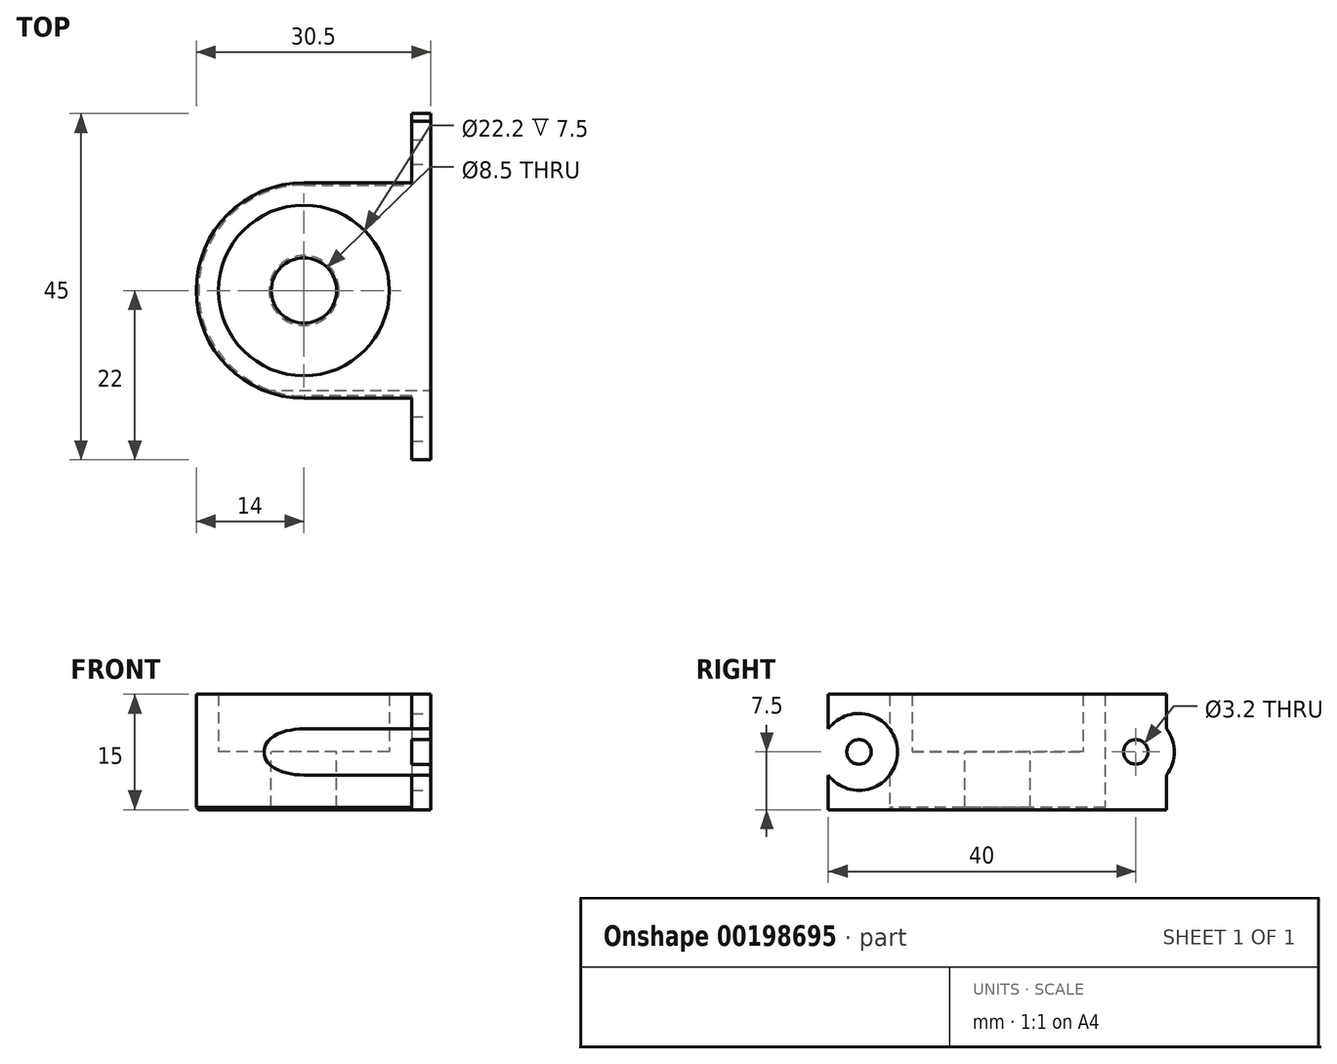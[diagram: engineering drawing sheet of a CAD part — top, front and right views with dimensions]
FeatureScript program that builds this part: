
annotation { "Feature Type Name" : "Feature", "Feature Type Description" : "" }
export const myFeature = defineFeature(function(context is Context, id is Id, definition is map)
    precondition{}
    {
        {
            var Q0;
            Q0=qCreatedBy(makeId("Top.planeOp"),FACE);
            var sketch = newSketch(context, id + "F0", { "sketchPlane" : qUnion([Q0])});
            skCircle(sketch, "E0", {"center": v(0, 0) * mm, "radius": 11.1 * mm});
            skCircle(sketch, "E1.0", {"center": v(0, 0) * mm, "radius": 14 * mm});
            skLineSegment(sketch, "E2", {"start": v(0, 14) * mm, "end": v(14, 14) * mm});
            skLineSegment(sketch, "E3", {"start": v(14, 14) * mm, "end": v(14, 22) * mm});
            skLineSegment(sketch, "E4", {"start": v(14, 22) * mm, "end": v(16.5, 22) * mm});
            skLineSegment(sketch, "E5", {"start": v(16.5, 22) * mm, "end": v(16.5, 0) * mm});
            skLineSegment(sketch, "E6.MirrorCS", {"start": v(16.5, -22) * mm, "end": v(16.5, 0) * mm});
            skLineSegment(sketch, "E7.MirrorCS", {"start": v(14, -14) * mm, "end": v(14, -22) * mm});
            skLineSegment(sketch, "E8.MirrorCS", {"start": v(14, -22) * mm, "end": v(16.5, -22) * mm});
            skLineSegment(sketch, "E9.MirrorCS", {"start": v(0, -14) * mm, "end": v(14, -14) * mm});
            skCircle(sketch, "E10", {"center": v(0, 0) * mm, "radius": 4.25 * mm});
            skSolve(sketch);
        }
        {
            var Q0;
            Q0=makeQuery(id+"F0.imprint","IMPRINT",FACE,{"disambiguationData":[TD([[makeQuery(id+"F0.imprint","IMPRINT",EDGE,{"derivedFrom":sQuery(id+"F0.wireOp",EDGE,"E0")}),-1.0]])]});
            var Q1;
            {var subQ0=sQuery(id+"F0.wireOp",EDGE,"E2");Q1=makeQuery(id+"F0.imprint","IMPRINT",FACE,{"disambiguationData":[TD([[makeQuery(id+"F0.imprint","IMPRINT",EDGE,{"derivedFrom":subQ0}),-1.0]])]});}
            extrude(context, id + "F1", {"entities" : qUnion([Q0, Q1]), "depth" : 7.5 * mm});
        }
        {
            var Q0;
            {var subQ0=sQuery(id+"F0.wireOp",EDGE,"E2");Q0=makeQuery(id+"F0.imprint","IMPRINT",FACE,{"disambiguationData":[TD([[makeQuery(id+"F0.imprint","IMPRINT",EDGE,{"derivedFrom":subQ0}),-1.0]])]});}
            var Q1;
            Q1=makeQuery(id+"F0.imprint","IMPRINT",FACE,{"disambiguationData":[TD([[makeQuery(id+"F0.imprint","IMPRINT",EDGE,{"derivedFrom":sQuery(id+"F0.wireOp",EDGE,"E0")}),-1.0]])]});
            var Q2;
            Q2=makeQuery(id+"F0.imprint","IMPRINT",FACE,{"disambiguationData":[TD([[makeQuery(id+"F0.imprint","IMPRINT",EDGE,{"derivedFrom":sQuery(id+"F0.wireOp",EDGE,"E0")}),1.0]])]});
            extrude(context, id + "F2", {"entities" : qUnion([Q0, Q1, Q2]), "operationType" : NewBodyOperationType.ADD, "oppositeDirection" : true, "depth" : 7.5 * mm});
        }
        {
            var Q0;
            {var subQ0=sQuery(id+"F0.wireOp",EDGE,"E6.MirrorCS");var subQ1=sQuery(id+"F0.wireOp",EDGE,"E5");Q0=makeQuery(id+"F2.boolean.opBoolean","MERGE",FACE,{"derivedFrom":[makeQuery(id+"F1.opExtrude","SWEPT_FACE",FACE,{"disambiguationData":[OSD([subQ1,subQ0])]}),makeQuery(id+"F2.opExtrude","SWEPT_FACE",FACE,{"disambiguationData":[OSD([subQ1,subQ0])]})]});}
            var sketch = newSketch(context, id + "F3", { "sketchPlane" : qUnion([Q0])});
            skLineSegment(sketch, "E11.0", {"start": v(14, 7.5) * mm, "end": v(22, 7.5) * mm, "construction": true});
            skLineSegment(sketch, "E12.0", {"start": v(14, -7.5) * mm, "end": v(22, -7.5) * mm, "construction": true});
            skLineSegment(sketch, "E13", {"start": v(18, -7.5) * mm, "end": v(18, 7.5) * mm, "construction": true});
            skCircle(sketch, "E14", {"center": v(18, 0) * mm, "radius": 1.6 * mm});
            skCircle(sketch, "E15.MirrorC", {"center": v(-18, 0) * mm, "radius": 1.6 * mm});
            skCircle(sketch, "E16", {"center": v(18, 0) * mm, "radius": 5 * mm});
            skCircle(sketch, "E17.MirrorC", {"center": v(-18, 0) * mm, "radius": 5 * mm});
            skSolve(sketch);
        }
        {
            var Q0;
            Q0=makeQuery(id+"F3.imprint","IMPRINT",FACE,{"disambiguationData":[TD([[makeQuery(id+"F3.imprint","IMPRINT",EDGE,{"derivedFrom":sQuery(id+"F3.wireOp",EDGE,"E14")}),1.0]])]});
            var Q1;
            Q1=makeQuery(id+"F3.imprint","IMPRINT",FACE,{"disambiguationData":[TD([[makeQuery(id+"F3.imprint","IMPRINT",EDGE,{"derivedFrom":sQuery(id+"F3.wireOp",EDGE,"E15.MirrorC")}),-1.0]])]});
            extrude(context, id + "F4", {"entities" : qUnion([Q0, Q1]), "operationType" : NewBodyOperationType.REMOVE, "endBound" : BoundingType.THROUGH_ALL, "oppositeDirection" : true, "depth" : 25 * mm});
        }
        {
            var Q0;
            Q0=makeQuery(id+"F2.opExtrude","CAP_FACE",FACE,{"disambiguationData":[OSD([sQuery(id+"F0.wireOp",EDGE,"E1.0"),sQuery(id+"F0.wireOp",EDGE,"E2"),sQuery(id+"F0.wireOp",EDGE,"E3"),sQuery(id+"F0.wireOp",EDGE,"E4"),sQuery(id+"F0.wireOp",EDGE,"E5"),sQuery(id+"F0.wireOp",EDGE,"E6.MirrorCS"),sQuery(id+"F0.wireOp",EDGE,"E7.MirrorCS"),sQuery(id+"F0.wireOp",EDGE,"E8.MirrorCS"),sQuery(id+"F0.wireOp",EDGE,"E9.MirrorCS"),sQuery(id+"F0.wireOp",EDGE,"E10")])],"isStart":false});
            chamfer(context, id + "F5", {"entities" : qUnion([Q0]), "width" : 0.3 * mm});
        }
        {
            var Q0;
            {var subQ0=sQuery(id+"F3.wireOp",EDGE,"E16");var subQ1=sQuery(id+"F0.wireOp",EDGE,"E5");var subQ2=sQuery(id+"F0.wireOp",EDGE,"E4");var subQ3=makeQuery(id+"F2.boolean.opBoolean","MERGE",EDGE,{"derivedFrom":[makeQuery(id+"F1.opExtrude","SWEPT_EDGE",EDGE,{"disambiguationData":[OSD([subQ2,subQ1])]}),makeQuery(id+"F2.opExtrude","SWEPT_EDGE",EDGE,{"disambiguationData":[OSD([subQ2,subQ1])]})]});var subQ4=makeQuery(id+"F3.imprint","INTERSECT",VERTEX,{"disambiguationData":[OD(0.0)],"derivedFrom":[subQ3,subQ0]});Q0=makeQuery(id+"F3.imprint","IMPRINT",FACE,{"disambiguationData":[TD([[makeQuery(id+"F3.imprint","IMPRINT",EDGE,{"disambiguationData":[TD([[subQ4,1.0]])],"derivedFrom":subQ0}),1.0]])]});}
            var Q1;
            {var subQ0=sQuery(id+"F3.wireOp",EDGE,"E17.MirrorC");var subQ1=sQuery(id+"F0.wireOp",EDGE,"E8.MirrorCS");var subQ2=sQuery(id+"F0.wireOp",EDGE,"E6.MirrorCS");var subQ3=makeQuery(id+"F2.boolean.opBoolean","MERGE",EDGE,{"derivedFrom":[makeQuery(id+"F1.opExtrude","SWEPT_EDGE",EDGE,{"disambiguationData":[OSD([subQ2,subQ1])]}),makeQuery(id+"F2.opExtrude","SWEPT_EDGE",EDGE,{"disambiguationData":[OSD([subQ2,subQ1])]})]});var subQ4=makeQuery(id+"F3.imprint","INTERSECT",VERTEX,{"disambiguationData":[OD(0.0)],"derivedFrom":[subQ3,subQ0]});Q1=makeQuery(id+"F3.imprint","IMPRINT",FACE,{"disambiguationData":[TD([[makeQuery(id+"F3.imprint","IMPRINT",EDGE,{"disambiguationData":[TD([[subQ4,1.0]])],"derivedFrom":subQ0}),-1.0]])]});}
            var Q2;
            {var subQ0=sQuery(id+"F0.wireOp",EDGE,"E3");Q2=makeQuery(id+"F2.boolean.opBoolean","MERGE",FACE,{"derivedFrom":[makeQuery(id+"F1.opExtrude","SWEPT_FACE",FACE,{"disambiguationData":[OSD([subQ0])]}),makeQuery(id+"F2.opExtrude","SWEPT_FACE",FACE,{"disambiguationData":[OSD([subQ0])]})]});}
            extrude(context, id + "F6", {"entities" : qUnion([Q0, Q1]), "operationType" : NewBodyOperationType.ADD, "endBound" : BoundingType.UP_TO_SURFACE, "oppositeDirection" : true, "endBoundEntityFace" : qUnion([Q2]), "depth" : 25 * mm});
        }
    });
